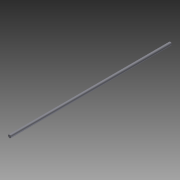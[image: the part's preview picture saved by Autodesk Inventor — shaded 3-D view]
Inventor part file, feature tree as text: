
AUTODESK INVENTOR PART (.ipt)
format: ipt  version: 2012 (Build 160160000, 160)  size: 83,968 bytes
history: native  units: in
note: dims shown in document units (in); Inventor stores cm internally (conversion verified against a paired STEP export)
features: imported_body x1, extrude x1, sketch x1
ambient origin geometry x8: Origin, YZ Plane, XZ Plane, XY Plane, X Axis, Y Axis, Z Axis, Center Point
bodies: Solid1 (feature_tree)
feature tree (3):
  imported_body  "Base1"
  extrude  "Extrusion1"  [1 undecoded]
  sketch  "Sketch1"  dims[d0=6.0in d1=0.0in]
note: 1 required parameter value undecoded (feature->parameter linkage not recoverable at this tier; creation-order binding heuristic only, values carry confidence <= 0.55)
